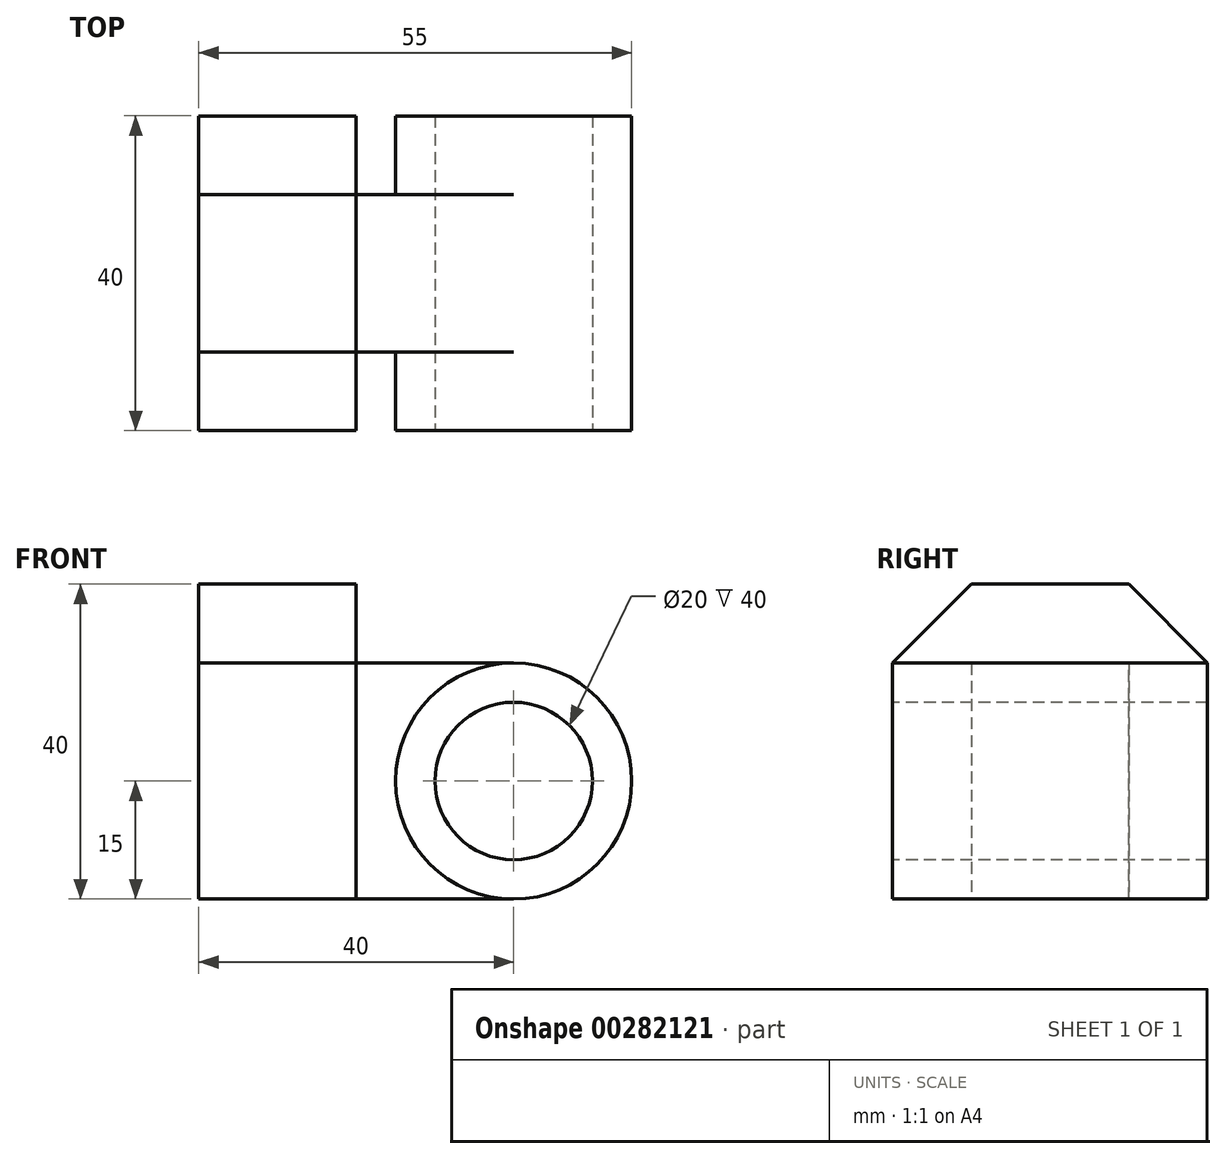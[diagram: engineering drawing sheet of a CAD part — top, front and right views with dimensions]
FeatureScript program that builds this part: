
annotation { "Feature Type Name" : "Feature", "Feature Type Description" : "" }
export const myFeature = defineFeature(function(context is Context, id is Id, definition is map)
    precondition{}
    {
        {
            var Q0;
            Q0=qCreatedBy(makeId("Right.planeOp"),FACE);
            var sketch = newSketch(context, id + "F0", { "sketchPlane" : qUnion([Q0])});
            skLineSegment(sketch, "E0", {"start": v(26.79, 0) * mm, "end": v(-13.21, 0) * mm});
            skLineSegment(sketch, "E1", {"start": v(-13.21, 0) * mm, "end": v(-13.21, 30) * mm});
            skLineSegment(sketch, "E2", {"start": v(-13.21, 30) * mm, "end": v(-3.21, 40) * mm});
            skLineSegment(sketch, "E3", {"start": v(-3.21, 40) * mm, "end": v(16.79, 40) * mm});
            skLineSegment(sketch, "E4", {"start": v(16.79, 40) * mm, "end": v(26.79, 30) * mm});
            skLineSegment(sketch, "E5", {"start": v(26.79, 30) * mm, "end": v(26.79, 0) * mm});
            skSolve(sketch);
        }
        {
            var Q0;
            Q0 = qSketchRegion(id + "F0", true);
            extrude(context, id + "F1", {"entities" : qUnion([Q0]), "oppositeDirection" : true, "depth" : 20 * mm});
        }
        {
            var Q0;
            Q0=makeQuery(id+"F1.opExtrude","CAP_FACE",FACE,{"disambiguationData":[OSD([sQuery(id+"F0.wireOp",EDGE,"E0"),sQuery(id+"F0.wireOp",EDGE,"E1"),sQuery(id+"F0.wireOp",EDGE,"E2"),sQuery(id+"F0.wireOp",EDGE,"E3"),sQuery(id+"F0.wireOp",EDGE,"E4"),sQuery(id+"F0.wireOp",EDGE,"E5")])],"isStart":true});
            var sketch = newSketch(context, id + "F2", { "sketchPlane" : qUnion([Q0])});
            skLineSegment(sketch, "E6", {"start": v(16.79, 0) * mm, "end": v(16.79, 30) * mm});
            skLineSegment(sketch, "E7", {"start": v(16.79, 30) * mm, "end": v(-3.21, 30) * mm});
            skLineSegment(sketch, "E8", {"start": v(-3.21, 30) * mm, "end": v(-3.21, 0) * mm});
            skLineSegment(sketch, "E9", {"start": v(-3.21, 0) * mm, "end": v(16.79, 0) * mm});
            skSolve(sketch);
        }
        {
            var Q0;
            Q0=makeQuery(id+"F2.imprint","IMPRINT",FACE,{"disambiguationData":[TD([[makeQuery(id+"F2.imprint","IMPRINT",EDGE,{"derivedFrom":sQuery(id+"F2.wireOp",EDGE,"E6")}),1.0]])]});
            extrude(context, id + "F3", {"entities" : qUnion([Q0]), "operationType" : NewBodyOperationType.ADD, "depth" : 20 * mm});
        }
        {
            var Q0;
            Q0=makeQuery(id+"F3.opExtrude","SWEPT_FACE",FACE,{"disambiguationData":[OSD([sQuery(id+"F2.wireOp",EDGE,"E8")])]});
            var sketch = newSketch(context, id + "F4", { "sketchPlane" : qUnion([Q0])});
            skLineSegment(sketch, "E10", {"start": v(0, 30) * mm, "end": v(20, 30) * mm});
            skLineSegment(sketch, "E11", {"start": v(0, 0) * mm, "end": v(20, 0) * mm});
            skArc(sketch, "E12", {"start": v(20, 30) * mm, "mid": v(35, 15) * mm, "end": v(20, 0) * mm});
            skCircle(sketch, "E13", {"center": v(20, 15) * mm, "radius": 15 * mm});
            skSolve(sketch);
        }
        {
            var Q0;
            Q0 = qSketchRegion(id + "F4", true);
            extrude(context, id + "F5", {"entities" : qUnion([Q0]), "operationType" : NewBodyOperationType.ADD, "depth" : 10 * mm});
        }
        {
            var Q0;
            Q0=makeQuery(id+"F5.opExtrude","CAP_FACE",FACE,{"disambiguationData":[OSD([sQuery(id+"F4.wireOp",EDGE,"E13")])],"isStart":false});
            extrude(context, id + "F6", {"entities" : qUnion([Q0]), "operationType" : NewBodyOperationType.ADD, "oppositeDirection" : true, "depth" : 40 * mm});
        }
        {
            var Q0;
            Q0=makeQuery(id+"F3.opExtrude","SWEPT_FACE",FACE,{"disambiguationData":[OSD([sQuery(id+"F2.wireOp",EDGE,"E8")])]});
            var sketch = newSketch(context, id + "F7", { "sketchPlane" : qUnion([Q0])});
            skCircle(sketch, "E14", {"center": v(20, 15) * mm, "radius": 10 * mm});
            skSolve(sketch);
        }
        {
            var Q0;
            Q0 = qSketchRegion(id + "F7", true);
            extrude(context, id + "F8", {"entities" : qUnion([Q0]), "operationType" : NewBodyOperationType.REMOVE, "endBound" : BoundingType.THROUGH_ALL, "oppositeDirection" : true, "depth" : 25 * mm});
        }
        {
            var Q0;
            Q0 = qSketchRegion(id + "F7", true);
            extrude(context, id + "F9", {"entities" : qUnion([Q0]), "operationType" : NewBodyOperationType.REMOVE, "endBound" : BoundingType.THROUGH_ALL, "depth" : 25 * mm});
        }
    });
